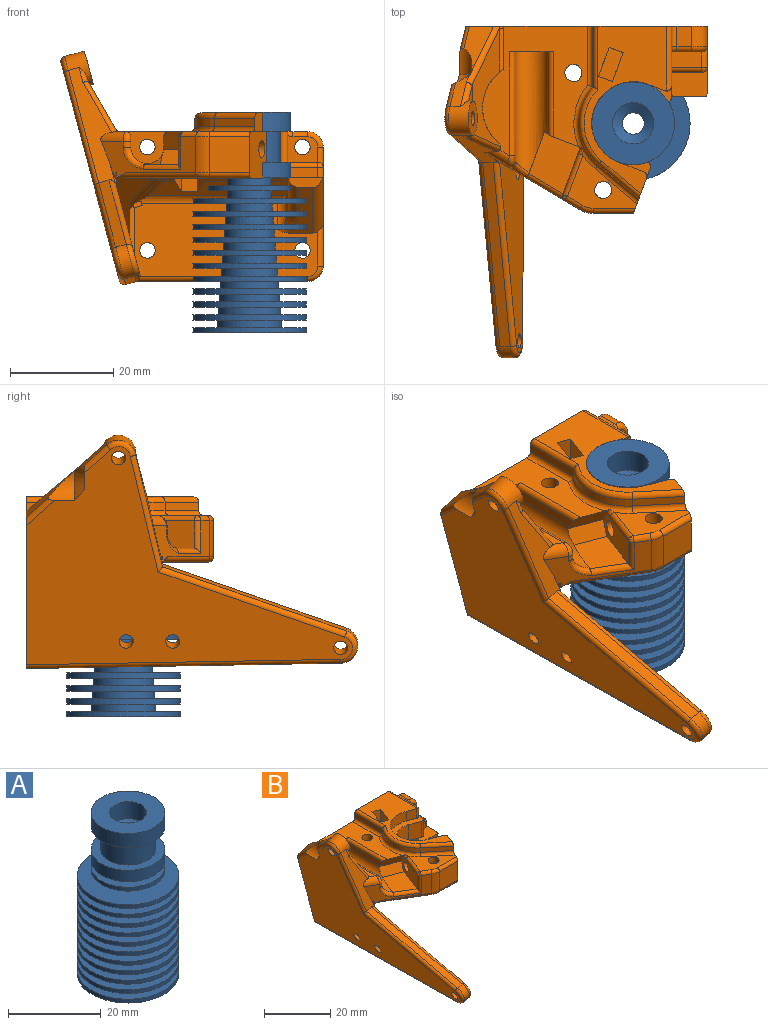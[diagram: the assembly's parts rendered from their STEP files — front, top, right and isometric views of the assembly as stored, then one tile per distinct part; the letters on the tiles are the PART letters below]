
ASSEMBLY  parts=2 mates=1
PART A: 62 faces, bbox 22x22x42.7 mm
  f0: cylinder r=3mm len=6mm, axis (0,0,-1), area 95mm2, adj f59,f60
  f1: cylinder r=2.1mm len=21.42mm, axis (0,0,1), area 282.6mm2, adj f57,f59
  f2: plane 22x22mm, normal (0,0,1), area 272.6mm2, adj f3,f56
  f3: cylinder r=5.85mm len=11.7mm, axis (0,0,1), area 55.1mm2, adj f2,f4
  f4: plane 22x22mm, normal (0,0,-1), area 272.6mm2, adj f3,f5
  f5: cylinder r=11mm len=22mm, axis (0,0,1), area 69.1mm2, adj f4,f6
  f6: plane 22x22mm, normal (0,0,1), area 279.8mm2, adj f5,f7
  f7: cylinder r=5.65mm len=11.3mm, axis (0,0,1), area 53.2mm2, adj f6,f8
  f8: plane 22x22mm, normal (0,0,-1), area 279.8mm2, adj f7,f9
  f9: cylinder r=11mm len=22mm, axis (0,0,1), area 69.1mm2, adj f8,f10
  f10: plane 22x22mm, normal (0,0,1), area 286.8mm2, adj f9,f11
  f11: cylinder r=5.45mm len=10.9mm, axis (0,0,1), area 51.4mm2, adj f10,f12
  f12: plane 22x22mm, normal (0,0,-1), area 286.8mm2, adj f11,f13
  f13: cylinder r=11mm len=22mm, axis (0,0,1), area 69.1mm2, adj f12,f14
  f14: plane 22x22mm, normal (0,0,1), area 293.5mm2, adj f13,f15
  f15: cylinder r=5.25mm len=10.5mm, axis (0,0,1), area 49.5mm2, adj f14,f16
  f16: plane 22x22mm, normal (0,0,-1), area 293.5mm2, adj f15,f17
  f17: cylinder r=11mm len=22mm, axis (0,0,1), area 69.1mm2, adj f16,f18
  f18: plane 22x22mm, normal (0,0,1), area 300mm2, adj f17,f19
  f19: cylinder r=5.05mm len=10.1mm, axis (0,0,1), area 47.6mm2, adj f18,f20
  f20: plane 22x22mm, normal (0,0,-1), area 300mm2, adj f19,f21
  f21: cylinder r=11mm len=22mm, axis (0,0,1), area 69.1mm2, adj f20,f22
  f22: plane 22x22mm, normal (0,0,1), area 306.2mm2, adj f21,f23
  f23: cylinder r=4.85mm len=9.7mm, axis (0,0,1), area 45.7mm2, adj f22,f24
  f24: plane 22x22mm, normal (0,0,-1), area 306.2mm2, adj f23,f25
  f25: cylinder r=11mm len=22mm, axis (0,0,1), area 69.1mm2, adj f24,f26
  f26: plane 22x22mm, normal (0,0,1), area 312.2mm2, adj f25,f27
  f27: cylinder r=4.65mm len=9.3mm, axis (0,0,1), area 43.8mm2, adj f26,f28
  f28: plane 22x22mm, normal (0,0,-1), area 312.2mm2, adj f27,f29
  f29: cylinder r=11mm len=22mm, axis (0,0,1), area 69.1mm2, adj f28,f30
  f30: plane 22x22mm, normal (0,0,1), area 317.9mm2, adj f29,f31
  f31: cylinder r=4.45mm len=8.9mm, axis (0,0,1), area 41.9mm2, adj f30,f32
  f32: plane 22x22mm, normal (0,0,-1), area 317.9mm2, adj f31,f33
  f33: cylinder r=11mm len=22mm, axis (0,0,1), area 69.1mm2, adj f32,f34
  f34: plane 22x22mm, normal (0,0,1), area 323.4mm2, adj f33,f35
  f35: cylinder r=4.25mm len=8.5mm, axis (0,0,1), area 40.1mm2, adj f34,f36
  f36: plane 16x16mm, normal (0,0,-1), area 144.3mm2, adj f35,f37
  f37: cylinder r=8mm len=16mm, axis (0,0,1), area 50.3mm2, adj f36,f38
  f38: plane 16x16mm, normal (0,0,1), area 144.3mm2, adj f37,f39
  f39: cylinder r=4.25mm len=8.5mm, axis (0,0,1), area 40.1mm2, adj f38,f40
  f40: plane 16x16mm, normal (0,0,-1), area 144.3mm2, adj f39,f41
  f41: cylinder r=8mm len=16mm, axis (0,0,1), area 150.8mm2, adj f40,f42
  f42: plane 16x16mm, normal (0,0,1), area 88mm2, adj f41,f43
  f43: cylinder r=6mm len=12mm, axis (0,0,1), area 226.2mm2, adj f42,f44
  f44: plane 16x16mm, normal (0,0,-1), area 88mm2, adj f43,f45
  f45: cylinder r=8mm len=16mm, axis (0,0,1), area 186mm2, adj f44,f46
  f46: plane 16x16mm, normal (0,0,1), area 150.8mm2, adj f45,f58
  f47: plane 22x22mm, normal (0,0,-1), area 349.9mm2, adj f48,f61
  f48: cylinder r=11mm len=22mm, axis (0,0,1), area 69.1mm2, adj f47,f49
  f49: plane 22x22mm, normal (0,0,1), area 257.4mm2, adj f48,f50
  f50: cylinder r=6.25mm len=12.5mm, axis (0,0,1), area 58.9mm2, adj f49,f51
  f51: plane 22x22mm, normal (0,0,-1), area 257.4mm2, adj f50,f52
  f52: cylinder r=11mm len=22mm, axis (0,0,1), area 69.1mm2, adj f51,f53
  f53: plane 22x22mm, normal (0,0,1), area 265.1mm2, adj f52,f54
  f54: cylinder r=6.05mm len=12.1mm, axis (0,0,1), area 57mm2, adj f53,f55
  f55: plane 22x22mm, normal (0,0,-1), area 265.1mm2, adj f54,f56
  f56: cylinder r=11mm len=22mm, axis (0,0,1), area 69.1mm2, adj f2,f55
  f57: cone r=0mm half-angle=59deg, axis (0,0,1), area 42.5mm2, adj f1,f58
  f58: cylinder r=4mm len=8mm, axis (0,0,1), area 113.1mm2, adj f46,f57
  f59: cone r=0mm half-angle=59deg, axis (0,0,-1), area 16.8mm2, adj f0,f1
  f60: cone r=0mm half-angle=59deg, axis (0,0,-1), area 2.2mm2, adj f0,f61
  f61: cylinder r=3.1mm len=10mm, axis (0,0,-1), area 194.8mm2, adj f47,f60
PART B: 178 faces, bbox 51.6x65.7x45.8 mm
  f0: plane 7.1x4.89mm, normal (-0.3,-0.81,-0.5), area 27.4mm2, adj f1,f5,f40,f44,f57,f77,f119,f172
  f1: bspline ~1.82x1.2mm, area 1.8mm2, adj f0,f2,f57,f172
  f2: cylinder r=1mm len=8.33mm, axis (-0.35,-0.94,0), area 13.4mm2, adj f1,f3,f23,f172
  f3: sphere r=1mm, area 0.9mm2, adj f2,f4,f96
  f4: cylinder r=1mm len=6.35mm, axis (0,0,-1), area 8.2mm2, adj f3,f62,f87,f172
  f5: cylinder r=1mm len=16.49mm, axis (0,-1,0), area 25.1mm2, adj f0,f44,f76,f119
  f6: bspline ~4.5x4.19mm, area 10.7mm2, adj f10,f77,f87,f101
  f7: bspline ~2.15x2mm, area 5.3mm2, adj f8,f75,f100,f101
  f8: cylinder r=2mm len=5.35mm, axis (0.86,-0.51,0), area 12.3mm2, adj f7,f9,f44,f87,f90
  f9: cylinder r=1mm len=10.1mm, axis (0.49,-0.22,-0.84), area 17.3mm2, adj f8,f44,f67,f90,f154
  f10: plane 10.02x3.82mm, normal (0.94,-0.35,0), area 4.8mm2, adj f6,f40,f62,f77,f87,f171
  f11: cylinder r=1mm len=3.6mm, axis (0,0,-1), area 6.4mm2, adj f23,f35,f113,f128,f133
  f12: torus R=9.5mm, axis (0,0,1), area 25.9mm2, adj f13,f22,f58,f133
  f13: cylinder r=1mm len=12.2mm, axis (0,1,0), area 18.9mm2, adj f12,f18,f109,f133
  f14: cylinder r=1.35mm len=4.66mm, axis (0.97,0,0.26), area 34.8mm2, adj f64,f78
  f15: plane 10.62x5.59mm, normal (0.94,-0.35,0), area 54.9mm2, adj f86,f133,f136,f159,f161
  f16: plane 4.46x2mm, normal (0,1,0), area 5mm2, adj f64,f69,f152
  f17: cylinder r=1mm len=12.07mm, axis (-0.35,-0.72,0.6), area 21.2mm2, adj f18,f19,f67,f68,f69,f89,f102,f112
  f18: plane 47.07x33.6mm, normal (0,1,0), area 1280.1mm2, adj f13,f17,f19,f27,f39,f44,f49,f51
  f19: bspline ~0.87x0.63mm, area 0.5mm2, adj f17,f18,f20,f44
  f20: cylinder r=1mm len=8.43mm, axis (0,-1,0), area 8.5mm2, adj f19,f42,f44,f67
  f21: cylinder r=1.65mm len=12.22mm, axis (0.94,-0.35,0), area 116.1mm2, adj f113,f160,f174
  f22: cylinder r=10.5mm len=15.06mm, axis (0,0,-1), area 27mm2, adj f12,f57,f109,f173
  f23: plane 24.46x20.19mm, normal (0,0,1), area 127.6mm2, adj f2,f11,f33,f34,f35,f56,f57,f88
  f24: cylinder r=1.35mm len=4.66mm, axis (0.97,0,0.26), area 34.8mm2, adj f64,f78
  f25: cylinder r=1mm len=33.38mm, axis (-1,0,0), area 51.7mm2, adj f36,f65,f82,f116,f135
  f26: cylinder r=3.3mm len=7.4mm, axis (-0.97,0,-0.26), area 42.2mm2, adj f66,f67,f71,f90,f102,f112,f118,f153
  f27: cylinder r=1mm len=11.8mm, axis (0,1,0), area 18.2mm2, adj f18,f44,f57,f109
  f28: plane 5.83x5.23mm, normal (0,-1,0), area 21.1mm2, adj f38,f43,f47,f53,f104,f113,f117
  f29: bspline ~5.61x2.88mm, area 6.8mm2, adj f45,f72,f97,f127
  f30: cylinder r=1mm len=14.97mm, axis (-0.86,0.51,0), area 26mm2, adj f72,f87,f97,f99
  f31: cylinder r=1mm len=1.5mm, axis (-0.86,0.51,0), area 1.1mm2, adj f63,f78,f79,f87
  f32: plane 4.8x3.08mm, normal (0.35,0.94,0), area 15.8mm2, adj f52,f97,f166,f176
  f33: cylinder r=8.05mm len=15.59mm, axis (0,0,-1), area 91mm2, adj f23,f35,f115,f133
  f34: plane 5.92x4.8mm, normal (0.35,0.94,0), area 30.4mm2, adj f23,f158,f175,f176
  f35: plane 3.6x3.28mm, normal (-0.35,-0.94,0), area 12.6mm2, adj f11,f23,f33,f133
  f36: cylinder r=1mm len=56.55mm, axis (0,-1,0.02), area 88.2mm2, adj f25,f37,f65,f78,f82
  f37: torus R=2.3mm, axis (-0.97,0,-0.26), area 12.9mm2, adj f36,f48,f78,f91
  f38: plane 5.83x3mm, normal (0,0,1), area 17.5mm2, adj f28,f113,f145,f146
  f39: plane 3.97x2.83mm, normal (0,0,1), area 11.2mm2, adj f18,f47,f51,f55
  f40: plane 7.71x4.27mm, normal (-0.3,-0.81,0.5), area 25.8mm2, adj f0,f10,f77,f171,f172
  f41: plane 19.25x5.41mm, normal (0.71,0,-0.71), area 109mm2, adj f45,f81,f105,f124,f127
  f42: cylinder r=9mm len=14.73mm, axis (0,0,-1), area 67.1mm2, adj f20,f44,f67
  f43: torus R=2mm, axis (0,-1,0), area 2.1mm2, adj f28,f47,f55,f113
  f44: plane 25.15x20.39mm, normal (0,0,1), area 232.7mm2, adj f0,f5,f8,f9,f18,f19,f20,f27
  f45: cylinder r=2mm len=14.49mm, axis (0,-1,0), area 22.8mm2, adj f29,f41,f97,f125
  f46: plane 5.84x5.76mm, normal (-1,0,0), area 14.4mm2, adj f61,f97,f103,f107,f122,f167,f169
  f47: cylinder r=1mm len=2.83mm, axis (1,0,0), area 4.4mm2, adj f28,f39,f43,f53
  f48: cylinder r=1mm len=35.97mm, axis (-0.09,0.94,0.33), area 59mm2, adj f37,f78,f90,f92
  f49: plane 23.01x12.74mm, normal (1,0,0), area 138.1mm2, adj f18,f51,f54,f61,f108,f117,f120,f143
  f50: plane 5.83x1.95mm, normal (0,-1,0), area 11.4mm2, adj f61,f113,f143,f146
  f51: cylinder r=3mm len=3.97mm, axis (0,1,0), area 18.7mm2, adj f18,f39,f49,f53
  f52: cylinder r=8.05mm len=15.59mm, axis (0,0,1), area 77.9mm2, adj f32,f97,f142,f176
  f53: torus R=2mm, axis (0,-1,0), area 6.5mm2, adj f28,f47,f51,f117
  f54: cylinder r=3mm len=3.97mm, axis (0,1,0), area 18.7mm2, adj f18,f49,f116,f135
  f55: cylinder r=1mm len=3.97mm, axis (0,-1,0), area 6.2mm2, adj f18,f39,f43,f113
  f56: cylinder r=1mm len=8.71mm, axis (-0.77,0.64,0), area 16.2mm2, adj f23,f57,f88,f173
  f57: torus R=11.5mm, axis (0,0,-1), area 26.3mm2, adj f0,f1,f22,f23,f27,f44,f56
  f58: cylinder r=1mm len=8.44mm, axis (-0.77,0.64,0), area 15.7mm2, adj f12,f88,f133,f173
  f59: plane 8.81x8.7mm, normal (0,-0.71,-0.7), area 37.8mm2, adj f60,f82,f103,f120,f121
  f60: plane 7.21x2.51mm, normal (0,-1,0), area 10.6mm2, adj f59,f61,f103,f120
  f61: plane 6.84x5.71mm, normal (0,0,1), area 32.3mm2, adj f46,f49,f50,f60,f103,f113,f120,f143
  f62: cylinder r=1mm len=7.97mm, axis (-0.86,0.51,0), area 12.5mm2, adj f4,f10,f87,f171,f172
  f63: plane 21.59x3.03mm, normal (-1,0,0), area 36.5mm2, adj f31,f70,f72,f78,f79,f87
  f64: plane 63.14x42.19mm, normal (-0.97,0,-0.26), area 1275.2mm2, adj f14,f16,f18,f24,f68,f69,f73,f74
  f65: plane 60.96x2.47mm, normal (0.26,-0.02,-0.97), area 127.4mm2, adj f18,f25,f36,f91,f135,f150
  f66: plane 6.6x6.38mm, normal (0.97,0,0.26), area 28.5mm2, adj f26,f74
  f67: plane 23.26x10.1mm, normal (0.87,0,0.5), area 105.7mm2, adj f9,f17,f20,f26,f42,f44,f71,f112
  f68: cylinder r=4.5mm len=5.75mm, axis (0,-1,0), area 21mm2, adj f17,f64,f69,f89,f151
  f69: cone r=2.5mm half-angle=45deg, axis (0,1,0), area 17.5mm2, adj f16,f17,f64,f68,f102,f152
  f70: plane 1.78x0.48mm, normal (0,-1,0), area 0.4mm2, adj f63,f78,f79
  f71: plane 4.12x2.57mm, normal (0.97,0,0.26), area 4.8mm2, adj f26,f67,f112
  f72: plane 13.5x12.68mm, normal (0,-0.68,-0.73), area 39mm2, adj f29,f30,f63,f78,f81,f87,f97,f127
  f73: cylinder r=1.35mm len=4.66mm, axis (0.97,0,0.26), area 34.8mm2, adj f64,f78
  f74: cylinder r=1.35mm len=5.47mm, axis (-0.97,0,-0.26), area 41.9mm2, adj f64,f66
  f75: plane 21.28x2mm, normal (1,0,0), area 42.3mm2, adj f7,f76,f77,f100,f101
  f76: plane 8.4x6.2mm, normal (0,-1,0), area 28.6mm2, adj f5,f44,f75,f77,f100,f119,f139
  f77: cylinder r=3.2mm len=23.43mm, axis (0,-1,0), area 196mm2, adj f0,f6,f10,f40,f75,f76,f119
  f78: plane 58.55x22.19mm, normal (0.97,0,0.26), area 650.2mm2, adj f14,f24,f31,f36,f37,f48,f63,f70
  f79: plane 20.17x0.48mm, normal (0,0,-1), area 9.6mm2, adj f31,f63,f70,f78
  f80: cylinder r=1.65mm len=14.34mm, axis (0.94,-0.35,0), area 145.9mm2, adj f134,f172
  f81: plane 15.8x6.86mm, normal (1,0,0), area 57.7mm2, adj f41,f72,f78,f105,f127
  f82: plane 35.85x14.53mm, normal (0,-1,0), area 440.5mm2, adj f25,f36,f59,f78,f83,f84,f105,f107
  f83: plane 1.71x0.46mm, normal (0.26,0,-0.97), area 0mm2, adj f82,f84,f85,f105
  f84: plane 0.83x0.22mm, normal (0.97,0,0.26), area 0mm2, adj f82,f83,f85,f123
  f85: plane 1.73x1.31mm, normal (0,-1,0), area 1.4mm2, adj f83,f84,f105,f123,f124
  f86: cylinder r=1.65mm len=8.32mm, axis (0.94,-0.35,0), area 79.3mm2, adj f15,f170
  f87: plane 18.31x10.93mm, normal (-0.51,-0.86,0), area 59.4mm2, adj f4,f6,f8,f10,f30,f31,f62,f63
  f88: plane 5.08x3.75mm, normal (0.94,-0.35,0), area 15.2mm2, adj f23,f56,f58,f133,f168,f173
  f89: plane 9.16x8.92mm, normal (-0.19,0.68,0.71), area 33.6mm2, adj f17,f18,f68,f151
  f90: plane 22.9x9.4mm, normal (-0.06,-0.97,0.22), area 72.2mm2, adj f8,f9,f26,f48,f78,f87,f92,f147
  f91: cylinder r=3.3mm len=6.73mm, axis (0.97,0,0.26), area 19.4mm2, adj f37,f65,f92,f149
  f92: plane 35.63x12.96mm, normal (-0.24,-0.34,0.91), area 79.5mm2, adj f48,f90,f91,f148
  f93: cylinder r=5mm len=7mm, axis (0,0,-1), area 18.8mm2, adj f87,f95,f99,f111
  f94: cylinder r=1mm len=8.15mm, axis (-1,0,0), area 12.5mm2, adj f23,f95,f111,f134
  f95: torus R=4mm, axis (0,0,1), area 3.9mm2, adj f23,f93,f94,f96
  f96: cylinder r=1mm len=3.42mm, axis (-0.86,0.51,0), area 5.3mm2, adj f3,f23,f87,f95
  f97: plane 31.23x25.42mm, normal (0,0,-1), area 302mm2, adj f29,f30,f32,f45,f46,f52,f72,f98
  f98: cylinder r=1mm len=8.15mm, axis (-1,0,0), area 12.5mm2, adj f97,f99,f111,f134
  f99: torus R=4mm, axis (0,0,-1), area 3.9mm2, adj f30,f93,f97,f98
  f100: cylinder r=1mm len=20.11mm, axis (0,1,0), area 31.6mm2, adj f7,f44,f75,f76
  f101: cylinder r=1mm len=1.51mm, axis (0,0,1), area 2.1mm2, adj f6,f7,f75,f87
  f102: plane 6.23x5.52mm, normal (-0.19,0.68,0.71), area 15.3mm2, adj f17,f26,f69,f112,f152
  f103: cylinder r=2mm len=7.71mm, axis (0,-0.7,0.71), area 26mm2, adj f46,f59,f60,f61,f121
  f104: cylinder r=1.5mm len=4.97mm, axis (0,-1,0), area 46.9mm2, adj f18,f28
  f105: cylinder r=1mm len=9.6mm, axis (0,0,1), area 10.6mm2, adj f41,f78,f81,f82,f83,f85,f124
  f106: cylinder r=1.65mm len=7mm, axis (0,0,1), area 72.6mm2, adj f23,f132
  f107: cylinder r=2mm len=7.81mm, axis (0,0,-1), area 13.7mm2, adj f46,f82,f121,f123,f169
  f108: cylinder r=1mm len=8.22mm, axis (0,0,-1), area 11.8mm2, adj f49,f82,f116,f120
  f109: plane 11.8x1.6mm, normal (-1,0,0), area 18.9mm2, adj f13,f18,f22,f27
  f110: plane 2.75x2mm, normal (0.87,-0.5,0), area 6.4mm2, adj f97,f131,f132,f141
  f111: plane 7.77x7mm, normal (0,-1,0), area 54.4mm2, adj f93,f94,f98,f134
  f112: cylinder r=1mm len=5.41mm, axis (0.18,0.73,-0.66), area 8mm2, adj f17,f26,f67,f71,f102
  f113: plane 14.1x11.92mm, normal (1,0,0), area 76.4mm2, adj f11,f18,f21,f23,f28,f38,f43,f50
  f114: plane 4.65x2.78mm, normal (0.87,-0.5,0), area 10.4mm2, adj f126,f137,f163,f165,f169
  f115: plane 4.8x3.6mm, normal (0.35,0.94,0), area 18.5mm2, adj f23,f33,f133,f168
  f116: torus R=2mm, axis (0,-1,0), area 6.5mm2, adj f25,f54,f82,f108
  f117: cylinder r=1mm len=3.96mm, axis (0,0,-1), area 5.4mm2, adj f28,f49,f53,f145
  f118: plane 0.92x0.78mm, normal (0.97,0,0.26), area 0.3mm2, adj f26,f67,f154
  f119: plane 15.5x2mm, normal (-1,0,0), area 29.8mm2, adj f0,f5,f76,f77
  f120: cylinder r=2mm len=11.18mm, axis (0,0.7,-0.71), area 40.2mm2, adj f49,f59,f60,f61,f82,f108
  f121: bspline ~5.46x4mm, area 12.5mm2, adj f59,f82,f103,f107
  f122: cylinder r=2mm len=16.25mm, axis (-1,0,0), area 25.2mm2, adj f46,f97,f155,f156,f169
  f123: cylinder r=2mm len=28.32mm, axis (-1,0,0), area 41.8mm2, adj f82,f84,f85,f107,f124,f169
  f124: cylinder r=2mm len=6.18mm, axis (-0.58,0.58,-0.58), area 14.1mm2, adj f41,f85,f105,f123,f125,f169
  f125: sphere r=2mm, area 1.2mm2, adj f45,f124,f126
  f126: cylinder r=2mm len=2.07mm, axis (-1,0,0), area 2.9mm2, adj f97,f114,f125,f137,f169
  f127: cylinder r=2mm len=7.24mm, axis (0.56,-0.6,0.56), area 17.3mm2, adj f29,f41,f72,f81
  f128: cylinder r=1mm len=12.57mm, axis (0,-1,0), area 19mm2, adj f11,f18,f113,f133
  f129: cylinder r=1.5mm len=4.97mm, axis (0,-1,0), area 46.9mm2, adj f18,f82
  f130: plane 3.18x2mm, normal (0,1,0), area 6.4mm2, adj f97,f131,f132,f138
  f131: plane 2.75x2mm, normal (0.87,0.5,0), area 6.4mm2, adj f97,f110,f130,f132
  f132: plane 6.35x5.5mm, normal (0,0,-1), area 17.6mm2, adj f106,f110,f130,f131,f138,f140,f141
  f133: plane 32.38x15.96mm, normal (0,0,1), area 181.3mm2, adj f11,f12,f13,f15,f18,f33,f35,f58
  f134: plane 9.16x8.82mm, normal (0.94,-0.35,0), area 68.1mm2, adj f23,f80,f94,f97,f98,f111,f166,f175
  f135: plane 33.38x3.97mm, normal (0,0,-1), area 132mm2, adj f18,f25,f54,f65
  f136: plane 6.61x4.82mm, normal (0,0,1), area 17.3mm2, adj f15,f159,f160,f161
  f137: plane 2.76x2.13mm, normal (0.87,0.5,0), area 6.4mm2, adj f97,f114,f126,f164,f165
  f138: plane 2.75x2mm, normal (-0.87,0.5,0), area 6.4mm2, adj f97,f130,f132,f140
  f139: cylinder r=1.5mm len=4.97mm, axis (0,-1,0), area 46.9mm2, adj f18,f76
  f140: plane 2.75x2mm, normal (-0.87,-0.5,0), area 6.4mm2, adj f97,f132,f138,f141
  f141: plane 3.18x2mm, normal (0,-1,0), area 6.4mm2, adj f97,f110,f132,f140
  f142: plane 3.28x3.08mm, normal (-0.35,-0.94,0), area 10.8mm2, adj f52,f97,f167,f176
  f143: cylinder r=1mm len=1.95mm, axis (0,0,-1), area 3.1mm2, adj f49,f50,f61,f144
  f144: sphere r=1mm, area 1mm2, adj f143,f145,f146
  f145: cylinder r=1mm len=4mm, axis (0,-1,0), area 5.5mm2, adj f38,f49,f117,f144
  f146: cylinder r=1mm len=5.83mm, axis (-1,0,0), area 9.2mm2, adj f38,f50,f113,f144
  f147: cylinder r=1mm len=22.8mm, axis (-0.25,0.23,0.94), area 36.8mm2, adj f64,f90,f148,f153
  f148: cylinder r=1mm len=36.48mm, axis (-0.09,0.94,0.33), area 59.9mm2, adj f64,f92,f147,f149
  f149: torus R=2.3mm, axis (0.97,0,0.26), area 12.9mm2, adj f64,f91,f148,f150
  f150: cylinder r=1mm len=60.87mm, axis (0,-1,0.02), area 95.6mm2, adj f18,f64,f65,f149
  f151: cylinder r=1mm len=6.12mm, axis (0.18,0.73,-0.66), area 10.5mm2, adj f18,f64,f68,f89
  f152: cylinder r=1mm len=5.62mm, axis (0.18,0.73,-0.66), area 9.9mm2, adj f16,f64,f69,f102,f153
  f153: torus R=2.3mm, axis (0.97,0,0.26), area 10.1mm2, adj f26,f64,f147,f152
  f154: cylinder r=1mm len=3.02mm, axis (-0.25,0.23,0.94), area 3mm2, adj f9,f26,f67,f90,f118
  f155: plane 2.76x2.13mm, normal (-0.87,0.5,0), area 6.4mm2, adj f97,f122,f156,f164,f165
  f156: plane 4.65x2.78mm, normal (-0.87,-0.5,0), area 10.4mm2, adj f122,f155,f163,f165,f169
  f157: cylinder r=1.5mm len=4.97mm, axis (0,-1,0), area 46.9mm2, adj f18,f82
  f158: cylinder r=6.05mm len=11.71mm, axis (0,0,1), area 112.5mm2, adj f23,f34,f162,f176
  f159: plane 10.62x2.71mm, normal (-0.35,-0.94,0), area 30.8mm2, adj f15,f133,f136,f160
  f160: plane 10.62x5.59mm, normal (-0.94,0.35,0), area 54.9mm2, adj f21,f133,f136,f159,f161
  f161: plane 10.62x2.71mm, normal (0.35,0.94,0), area 30.8mm2, adj f15,f133,f136,f160
  f162: plane 5.92x3.98mm, normal (-0.35,-0.94,0), area 25.2mm2, adj f23,f158,f174,f176
  f163: plane 4.62x3.18mm, normal (0,-1,0), area 14.7mm2, adj f114,f156,f165,f169
  f164: plane 3.18x2mm, normal (0,1,0), area 6.4mm2, adj f97,f137,f155,f165
  f165: plane 6.35x5.5mm, normal (0,0,-1), area 17.6mm2, adj f114,f137,f155,f156,f163,f164,f177
  f166: cylinder r=1mm len=3.08mm, axis (0,0,1), area 4.8mm2, adj f32,f97,f134,f176
  f167: cylinder r=1mm len=3.08mm, axis (0,0,-1), area 5.9mm2, adj f46,f97,f113,f142,f176
  f168: cylinder r=1mm len=3.6mm, axis (0,0,-1), area 5.7mm2, adj f23,f88,f115,f133
  f169: plane 26.79x2.95mm, normal (0,-0.71,-0.71), area 88.1mm2, adj f46,f107,f114,f122,f123,f124,f126,f156
  f170: plane 3.3x3.09mm, normal (0.94,-0.35,0), area 8.6mm2, adj f86
  f171: plane 11.83x10.03mm, normal (0,0,1), area 68.8mm2, adj f10,f40,f62,f172
  f172: plane 10.96x5.78mm, normal (-0.94,0.35,0), area 50.1mm2, adj f0,f1,f2,f4,f40,f62,f80,f171
  f173: plane 7.8x6.51mm, normal (-0.64,-0.77,0), area 16.3mm2, adj f22,f56,f58,f88
  f174: cylinder r=1mm len=5.92mm, axis (0,0,-1), area 11.4mm2, adj f21,f23,f113,f162,f176
  f175: cylinder r=1mm len=5.92mm, axis (0,0,1), area 9.3mm2, adj f23,f34,f134,f176
  f176: plane 18.68x15.51mm, normal (0,0,-1), area 67.2mm2, adj f32,f34,f52,f113,f134,f142,f158,f162
  f177: cylinder r=1.65mm len=7mm, axis (0,0,1), area 72.6mm2, adj f44,f165
PLACE A t=(-70.65,7.66,73.23)mm
PLACE B t=(27.84,-41.13,35.23)mm fixed
MATE fastened A.f0 <-> B.f12  axis (0,0,1) through (-70.65,7.66,66.53)mm
